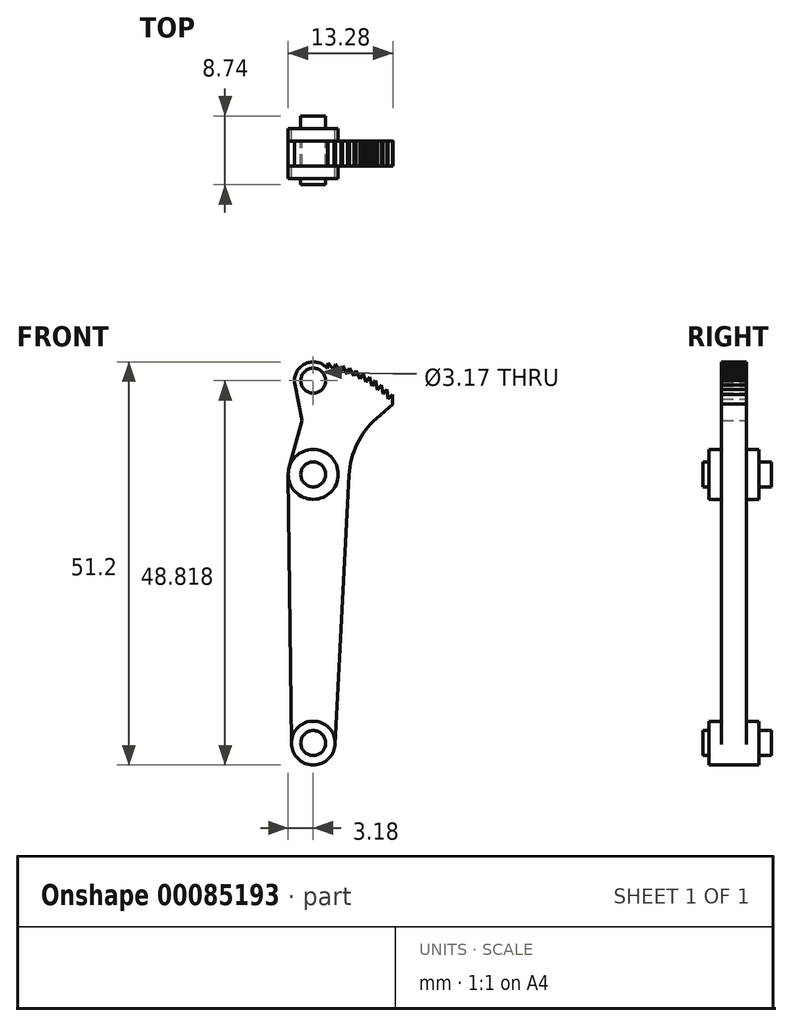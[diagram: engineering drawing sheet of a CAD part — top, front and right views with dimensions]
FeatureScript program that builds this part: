
annotation { "Feature Type Name" : "Feature", "Feature Type Description" : "" }
export const myFeature = defineFeature(function(context is Context, id is Id, definition is map)
    precondition{}
    {
        {
            var Q0;
            Q0=qCreatedBy(makeId("Front.planeOp"),FACE);
            var sketch = newSketch(context, id + "F0", { "sketchPlane" : qUnion([Q0])});
            skArc(sketch, "E0", {"start": v(-2.78, -0.03) * mm, "mid": v(0.02, -2.78) * mm, "end": v(2.78, 0) * mm});
            skLineSegment(sketch, "E1", {"start": v(0, 0) * mm, "end": v(0, 34.13) * mm, "construction": true});
            skArc(sketch, "E2", {"start": v(-3.06, 34.98) * mm, "mid": v(-3.15, 34.54) * mm, "end": v(-3.17, 34.1) * mm});
            skLineSegment(sketch, "E3", {"start": v(0, 34.13) * mm, "end": v(0, 48.42) * mm, "construction": true});
            skArc(sketch, "E4", {"start": v(1.8, 47.58) * mm, "mid": v(-1.05, 48.18) * mm, "end": v(-2.33, 45.56) * mm});
            skCircle(sketch, "E5", {"center": v(0, 46.04) * mm, "radius": 1.59 * mm});
            skLineSegment(sketch, "E6.trimOffspring", {"start": v(-1.4, 40.98) * mm, "end": v(-3.06, 34.98) * mm});
            skLineSegment(sketch, "E7.trimOffspring", {"start": v(-1.4, 40.98) * mm, "end": v(-2.33, 45.56) * mm});
            skLineSegment(sketch, "E8", {"start": v(-1.4, 40.98) * mm, "end": v(0, 34.13) * mm, "construction": true});
            skLineSegment(sketch, "E9", {"start": v(0, 46.04) * mm, "end": v(-1.4, 40.98) * mm, "construction": true});
            skLineSegment(sketch, "E10", {"start": v(-3.17, 34.1) * mm, "end": v(-2.78, -0.03) * mm});
            skLineSegment(sketch, "E11", {"start": v(2.77, -0.15) * mm, "end": v(4.8, 38.38) * mm});
            skLineSegment(sketch, "E12", {"start": v(0, 0) * mm, "end": v(26.23, 0) * mm, "construction": true});
            skArc(sketch, "E13.trimOffspring", {"start": v(10.1, 43.08) * mm, "mid": v(10.1, 43.09) * mm, "end": v(10.08, 43.1) * mm});
            skLineSegment(sketch, "E14", {"start": v(0, 34.13) * mm, "end": v(1.8, 47.58) * mm, "construction": true});
            skLineSegment(sketch, "E15", {"start": v(1.9, 48.3) * mm, "end": v(1.8, 47.58) * mm});
            skLineSegment(sketch, "E16", {"start": v(1.9, 48.3) * mm, "end": v(2.66, 47.36) * mm});
            skLineSegment(sketch, "E17.trimOffspring", {"start": v(2.66, 47.36) * mm, "end": v(2.81, 48.14) * mm});
            skLineSegment(sketch, "E18", {"start": v(2.81, 48.14) * mm, "end": v(3.5, 47.16) * mm});
            skLineSegment(sketch, "E19", {"start": v(3.71, 47.93) * mm, "end": v(4.34, 46.9) * mm});
            skLineSegment(sketch, "E20", {"start": v(4.6, 47.66) * mm, "end": v(5.16, 46.6) * mm});
            skLineSegment(sketch, "E21", {"start": v(5.46, 47.33) * mm, "end": v(5.95, 46.24) * mm});
            skLineSegment(sketch, "E22", {"start": v(6.3, 46.95) * mm, "end": v(6.72, 45.83) * mm});
            skLineSegment(sketch, "E23", {"start": v(7.11, 46.52) * mm, "end": v(7.46, 45.38) * mm});
            skLineSegment(sketch, "E24", {"start": v(7.9, 46.04) * mm, "end": v(8.17, 44.87) * mm});
            skLineSegment(sketch, "E25", {"start": v(8.65, 45.5) * mm, "end": v(8.85, 44.32) * mm});
            skLineSegment(sketch, "E26", {"start": v(9.37, 44.92) * mm, "end": v(9.49, 43.73) * mm});
            skLineSegment(sketch, "E27", {"start": v(10.04, 44.3) * mm, "end": v(10.08, 43.1) * mm});
            skLineSegment(sketch, "E28.trimOffspring", {"start": v(3.5, 47.16) * mm, "end": v(3.71, 47.93) * mm});
            skLineSegment(sketch, "E29.trimOffspring", {"start": v(4.34, 46.9) * mm, "end": v(4.6, 47.66) * mm});
            skLineSegment(sketch, "E30.trimOffspring", {"start": v(5.16, 46.6) * mm, "end": v(5.46, 47.33) * mm});
            skLineSegment(sketch, "E31.trimOffspring", {"start": v(5.95, 46.24) * mm, "end": v(6.3, 46.95) * mm});
            skLineSegment(sketch, "E32.trimOffspring", {"start": v(6.72, 45.83) * mm, "end": v(7.11, 46.52) * mm});
            skLineSegment(sketch, "E33.trimOffspring", {"start": v(7.46, 45.38) * mm, "end": v(7.9, 46.04) * mm});
            skLineSegment(sketch, "E34.trimOffspring", {"start": v(8.17, 44.87) * mm, "end": v(8.65, 45.5) * mm});
            skLineSegment(sketch, "E35.trimOffspring", {"start": v(8.85, 44.32) * mm, "end": v(9.37, 44.92) * mm});
            skLineSegment(sketch, "E36.trimOffspring", {"start": v(9.49, 43.73) * mm, "end": v(10.04, 44.3) * mm});
            skLineSegment(sketch, "E37.trimOffspring", {"start": v(4.8, 38.38) * mm, "end": v(10.1, 43.08) * mm});
            skSolve(sketch);
        }
        {
            var Q0;
            Q0=makeQuery(id+"F0.imprint","IMPRINT",FACE,{"disambiguationData":[TD([[makeQuery(id+"F0.imprint","IMPRINT",EDGE,{"derivedFrom":sQuery(id+"F0.wireOp",EDGE,"E2")}),1.0]])]});
            extrude(context, id + "F1", {"entities" : qUnion([Q0]), "depth" : 3.17 * mm});
        }
        {
            var Q0;
            Q0=makeQuery(id+"F1.opExtrude","CAP_FACE",FACE,{"disambiguationData":[OSD([sQuery(id+"F0.wireOp",EDGE,"E0"),sQuery(id+"F0.wireOp",EDGE,"E2"),sQuery(id+"F0.wireOp",EDGE,"E4"),sQuery(id+"F0.wireOp",EDGE,"E5"),sQuery(id+"F0.wireOp",EDGE,"E6.trimOffspring"),sQuery(id+"F0.wireOp",EDGE,"E7.trimOffspring"),sQuery(id+"F0.wireOp",EDGE,"E10"),sQuery(id+"F0.wireOp",EDGE,"E11"),sQuery(id+"F0.wireOp",EDGE,"E13.trimOffspring"),sQuery(id+"F0.wireOp",EDGE,"E15"),sQuery(id+"F0.wireOp",EDGE,"E16"),sQuery(id+"F0.wireOp",EDGE,"E17.trimOffspring"),sQuery(id+"F0.wireOp",EDGE,"E18"),sQuery(id+"F0.wireOp",EDGE,"E19"),sQuery(id+"F0.wireOp",EDGE,"E20"),sQuery(id+"F0.wireOp",EDGE,"E21"),sQuery(id+"F0.wireOp",EDGE,"E22"),sQuery(id+"F0.wireOp",EDGE,"E23"),sQuery(id+"F0.wireOp",EDGE,"E24"),sQuery(id+"F0.wireOp",EDGE,"E25"),sQuery(id+"F0.wireOp",EDGE,"E26"),sQuery(id+"F0.wireOp",EDGE,"E27"),sQuery(id+"F0.wireOp",EDGE,"E28.trimOffspring"),sQuery(id+"F0.wireOp",EDGE,"E29.trimOffspring"),sQuery(id+"F0.wireOp",EDGE,"E30.trimOffspring"),sQuery(id+"F0.wireOp",EDGE,"E31.trimOffspring"),sQuery(id+"F0.wireOp",EDGE,"E32.trimOffspring"),sQuery(id+"F0.wireOp",EDGE,"E33.trimOffspring"),sQuery(id+"F0.wireOp",EDGE,"E34.trimOffspring"),sQuery(id+"F0.wireOp",EDGE,"E35.trimOffspring"),sQuery(id+"F0.wireOp",EDGE,"E36.trimOffspring"),sQuery(id+"F0.wireOp",EDGE,"E37.trimOffspring")])],"isStart":false});
            var sketch = newSketch(context, id + "F2", { "sketchPlane" : qUnion([Q0])});
            skCircle(sketch, "E38", {"center": v(0, 0) * mm, "radius": 2.78 * mm});
            skCircle(sketch, "E39", {"center": v(0, 34.13) * mm, "radius": 3.18 * mm});
            skSolve(sketch);
        }
        {
            var Q0;
            Q0 = qSketchRegion(id + "F2", true);
            extrude(context, id + "F3", {"entities" : qUnion([Q0]), "operationType" : NewBodyOperationType.ADD, "depth" : 1.59 * mm});
        }
        {
            var Q0;
            Q0=makeQuery(id+"F1.opExtrude","CAP_FACE",FACE,{"disambiguationData":[OSD([sQuery(id+"F0.wireOp",EDGE,"E0"),sQuery(id+"F0.wireOp",EDGE,"E2"),sQuery(id+"F0.wireOp",EDGE,"E4"),sQuery(id+"F0.wireOp",EDGE,"E5"),sQuery(id+"F0.wireOp",EDGE,"E6.trimOffspring"),sQuery(id+"F0.wireOp",EDGE,"E7.trimOffspring"),sQuery(id+"F0.wireOp",EDGE,"E10"),sQuery(id+"F0.wireOp",EDGE,"E11"),sQuery(id+"F0.wireOp",EDGE,"E13.trimOffspring"),sQuery(id+"F0.wireOp",EDGE,"E15"),sQuery(id+"F0.wireOp",EDGE,"E16"),sQuery(id+"F0.wireOp",EDGE,"E17.trimOffspring"),sQuery(id+"F0.wireOp",EDGE,"E18"),sQuery(id+"F0.wireOp",EDGE,"E19"),sQuery(id+"F0.wireOp",EDGE,"E20"),sQuery(id+"F0.wireOp",EDGE,"E21"),sQuery(id+"F0.wireOp",EDGE,"E22"),sQuery(id+"F0.wireOp",EDGE,"E23"),sQuery(id+"F0.wireOp",EDGE,"E24"),sQuery(id+"F0.wireOp",EDGE,"E25"),sQuery(id+"F0.wireOp",EDGE,"E26"),sQuery(id+"F0.wireOp",EDGE,"E27"),sQuery(id+"F0.wireOp",EDGE,"E28.trimOffspring"),sQuery(id+"F0.wireOp",EDGE,"E29.trimOffspring"),sQuery(id+"F0.wireOp",EDGE,"E30.trimOffspring"),sQuery(id+"F0.wireOp",EDGE,"E31.trimOffspring"),sQuery(id+"F0.wireOp",EDGE,"E32.trimOffspring"),sQuery(id+"F0.wireOp",EDGE,"E33.trimOffspring"),sQuery(id+"F0.wireOp",EDGE,"E34.trimOffspring"),sQuery(id+"F0.wireOp",EDGE,"E35.trimOffspring"),sQuery(id+"F0.wireOp",EDGE,"E36.trimOffspring"),sQuery(id+"F0.wireOp",EDGE,"E37.trimOffspring")])],"isStart":true});
            var sketch = newSketch(context, id + "F4", { "sketchPlane" : qUnion([Q0])});
            skCircle(sketch, "E40", {"center": v(0, 0) * mm, "radius": 2.78 * mm});
            skLineSegment(sketch, "E41", {"start": v(0, 0) * mm, "end": v(0, 34.13) * mm});
            skCircle(sketch, "E42", {"center": v(0, 34.13) * mm, "radius": 3.17 * mm});
            skSolve(sketch);
        }
        {
            var Q0;
            Q0 = qSketchRegion(id + "F4", true);
            extrude(context, id + "F5", {"entities" : qUnion([Q0]), "operationType" : NewBodyOperationType.ADD, "depth" : 1.59 * mm});
        }
        {
            var Q0;
            Q0=makeQuery(id+"F3.opExtrude","CAP_FACE",FACE,{"disambiguationData":[OSD([sQuery(id+"F2.wireOp",EDGE,"E38")])],"isStart":false});
            var sketch = newSketch(context, id + "F6", { "sketchPlane" : qUnion([Q0])});
            skCircle(sketch, "E43", {"center": v(0, 0) * mm, "radius": 1.59 * mm});
            skCircle(sketch, "E44", {"center": v(0, 34.13) * mm, "radius": 1.59 * mm});
            skSolve(sketch);
        }
        {
            var Q0;
            Q0 = qSketchRegion(id + "F6", true);
            extrude(context, id + "F7", {"entities" : qUnion([Q0]), "operationType" : NewBodyOperationType.ADD, "depth" : 0.8 * mm});
        }
        {
            var Q0;
            Q0=makeQuery(id+"F5.opExtrude","CAP_FACE",FACE,{"disambiguationData":[OSD([sQuery(id+"F4.wireOp",EDGE,"E40")])],"isStart":false});
            var sketch = newSketch(context, id + "F8", { "sketchPlane" : qUnion([Q0])});
            skCircle(sketch, "E45", {"center": v(0, 0) * mm, "radius": 1.59 * mm});
            skCircle(sketch, "E46", {"center": v(0, 34.13) * mm, "radius": 1.59 * mm});
            skSolve(sketch);
        }
        {
            var Q0;
            Q0 = qSketchRegion(id + "F8", true);
            extrude(context, id + "F9", {"entities" : qUnion([Q0]), "operationType" : NewBodyOperationType.ADD, "depth" : 1.59 * mm});
        }
        {
            var Q0;
            Q0=makeQuery(id+"F1.opExtrude","SWEPT_EDGE",EDGE,{"disambiguationData":[OSD([sQuery(id+"F0.wireOp",EDGE,"E11"),sQuery(id+"F0.wireOp",EDGE,"E37.trimOffspring")])]});
            fillet(context, id + "F10", {"entities" : qUnion([Q0]), "radius" : 10.32 * mm, "tangentPropagation" : true, "allowEdgeOverflow" : false});
        }
    });
